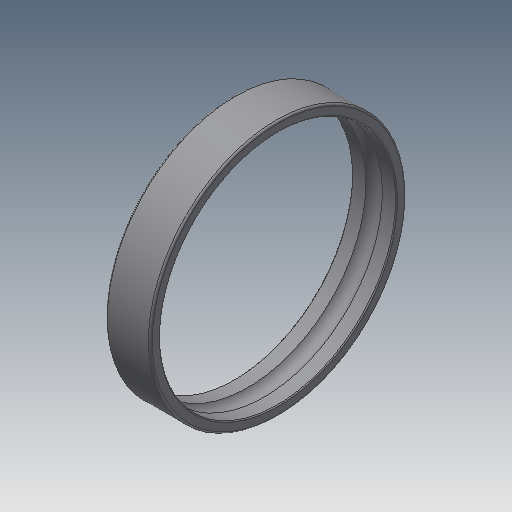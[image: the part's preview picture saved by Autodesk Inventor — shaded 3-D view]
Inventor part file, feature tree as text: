
AUTODESK INVENTOR PART (.ipt)
format: ipt  version: 2019.4 (Build 234330000, 330)  size: 178,176 bytes
history: native  units: mm
features: other x7, revolve x1, sketch x1
ambient origin geometry x8: Origin, YZ Plane, XZ Plane, XY Plane, X Axis, Y Axis, Z Axis, Center Point
bodies: Solid1 (feature_tree)
feature tree (9):
  revolve  "Revolution1"  [1 undecoded]
  other  "1_XY"
  other  "1_YZ"
  other  "1_ZX"
  other  "1_X"
  other  "1_Y"
  other  "1_Z"
  other  "1_Center"
  sketch  "Sketch_1"  dims[d0=360.0deg]
note: 1 required parameter value undecoded (feature->parameter linkage not recoverable at this tier; creation-order binding heuristic only, values carry confidence <= 0.55)
